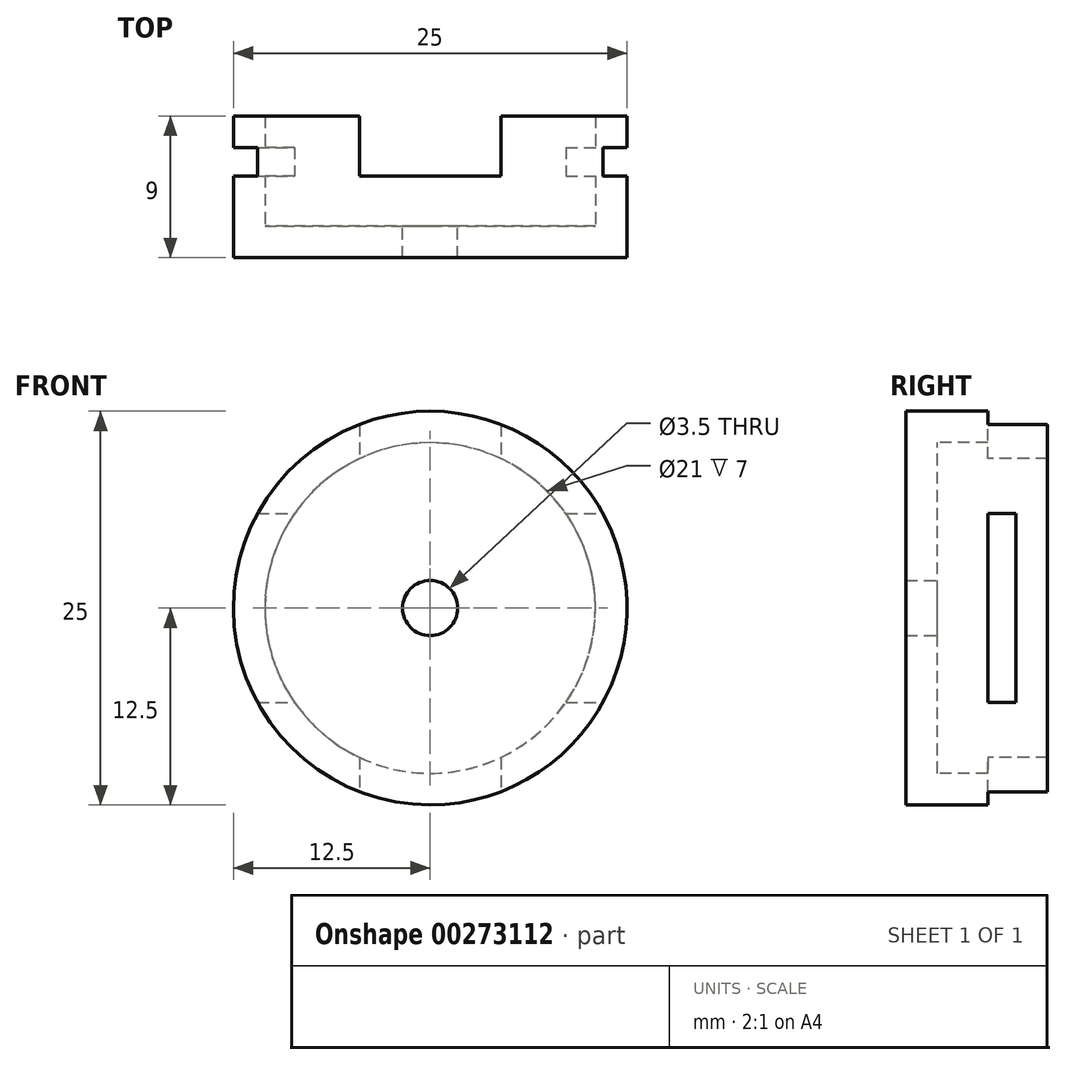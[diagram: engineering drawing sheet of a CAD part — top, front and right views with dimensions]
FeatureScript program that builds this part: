
annotation { "Feature Type Name" : "Feature", "Feature Type Description" : "" }
export const myFeature = defineFeature(function(context is Context, id is Id, definition is map)
    precondition{}
    {
        {
            var Q0;
            Q0=qCreatedBy(makeId("Front.planeOp"),FACE);
            var sketch = newSketch(context, id + "F0", { "sketchPlane" : qUnion([Q0])});
            skCircle(sketch, "E0", {"center": v(0, 0) * mm, "radius": 10.5 * mm});
            skCircle(sketch, "E1", {"center": v(0, 0) * mm, "radius": 12.5 * mm});
            skCircle(sketch, "E2", {"center": v(0, 0) * mm, "radius": 1.75 * mm});
            skSolve(sketch);
        }
        {
            var Q0;
            Q0=makeQuery(id+"F0.imprint","IMPRINT",FACE,{"disambiguationData":[TD([[makeQuery(id+"F0.imprint","IMPRINT",EDGE,{"derivedFrom":sQuery(id+"F0.wireOp",EDGE,"E0")}),1.0]])]});
            var Q1;
            Q1=makeQuery(id+"F0.imprint","IMPRINT",FACE,{"disambiguationData":[TD([[makeQuery(id+"F0.imprint","IMPRINT",EDGE,{"derivedFrom":sQuery(id+"F0.wireOp",EDGE,"E0")}),-1.0]])]});
            extrude(context, id + "F1", {"entities" : qUnion([Q0, Q1]), "depth" : 2 * mm});
        }
        {
            var Q0;
            Q0 = qSketchRegion(id + "F0", true);
            extrude(context, id + "F2", {"entities" : qUnion([Q0]), "operationType" : NewBodyOperationType.ADD, "oppositeDirection" : true, "depth" : 7 * mm});
        }
        {
            var Q0;
            Q0=qCreatedBy(makeId("Top.planeOp"),FACE);
            var sketch = newSketch(context, id + "F3", { "sketchPlane" : qUnion([Q0])});
            skLineSegment(sketch, "E3.bottom", {"start": v(-15, 5) * mm, "end": v(15, 5) * mm});
            skLineSegment(sketch, "E3.top", {"start": v(-15, 3.2) * mm, "end": v(15, 3.2) * mm});
            skLineSegment(sketch, "E3.left", {"start": v(-15, 5) * mm, "end": v(-15, 3.2) * mm});
            skLineSegment(sketch, "E3.right", {"start": v(15, 5) * mm, "end": v(15, 3.2) * mm});
            skLineSegment(sketch, "E4.bottom", {"start": v(-4.5, 10.84) * mm, "end": v(4.5, 10.84) * mm});
            skLineSegment(sketch, "E4.top", {"start": v(-4.5, 3) * mm, "end": v(4.5, 3) * mm});
            skLineSegment(sketch, "E4.left", {"start": v(-4.5, 10.84) * mm, "end": v(-4.5, 3) * mm});
            skLineSegment(sketch, "E4.right", {"start": v(4.5, 10.84) * mm, "end": v(4.5, 3) * mm});
            skSolve(sketch);
        }
        {
            var Q0;
            {var subQ0=sQuery(id+"F3.wireOp",EDGE,"E4.left");var subQ1=sQuery(id+"F3.wireOp",EDGE,"E3.bottom");var subQ2=makeQuery(id+"F3.imprint","INTERSECT",VERTEX,{"derivedFrom":[subQ1,subQ0]});Q0=makeQuery(id+"F3.imprint","IMPRINT",FACE,{"disambiguationData":[TD([[makeQuery(id+"F3.imprint","IMPRINT",EDGE,{"disambiguationData":[TD([[subQ2,-1.0]])],"derivedFrom":subQ1}),-1.0]])]});}
            var Q1;
            {var subQ5=sQuery(id+"F3.wireOp",EDGE,"E4.bottom");Q1=makeQuery(id+"F3.imprint","IMPRINT",FACE,{"disambiguationData":[TD([[makeQuery(id+"F3.imprint","IMPRINT",EDGE,{"derivedFrom":subQ5}),-1.0]])]});}
            extrude(context, id + "F4", {"entities" : qUnion([Q0, Q1]), "operationType" : NewBodyOperationType.REMOVE, "endBound" : BoundingType.SYMMETRIC, "oppositeDirection" : true, "depth" : 30 * mm});
        }
        {
            var Q0;
            Q0 = qSketchRegion(id + "F3", true);
            extrude(context, id + "F5", {"entities" : qUnion([Q0]), "operationType" : NewBodyOperationType.REMOVE, "endBound" : BoundingType.SYMMETRIC, "depth" : 12 * mm});
        }
    });
